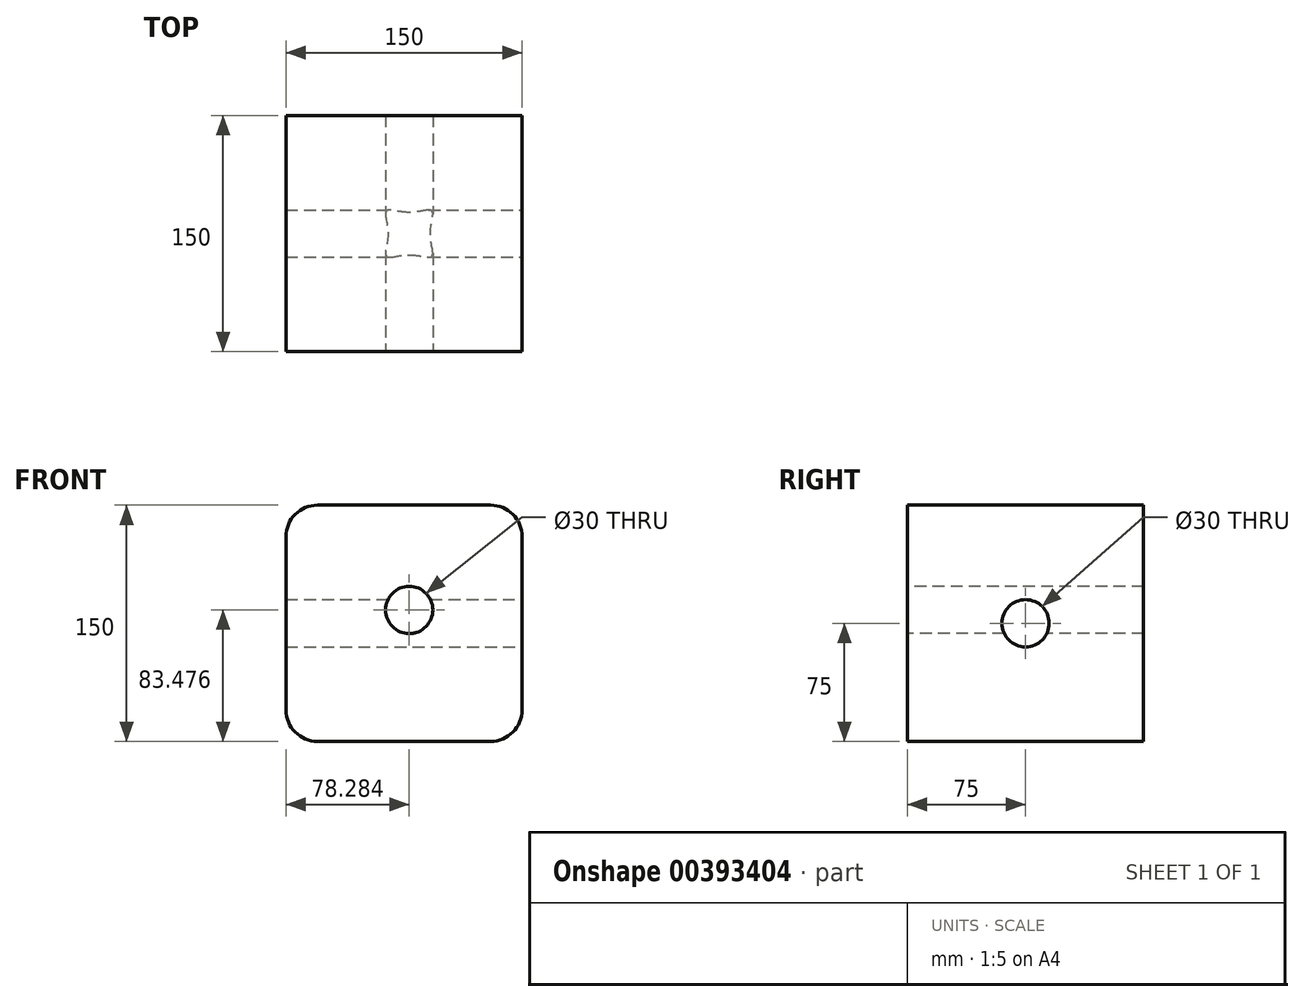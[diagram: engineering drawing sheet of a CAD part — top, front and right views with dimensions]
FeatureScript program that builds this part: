
annotation { "Feature Type Name" : "Feature", "Feature Type Description" : "" }
export const myFeature = defineFeature(function(context is Context, id is Id, definition is map)
    precondition{}
    {
        {
            var Q0;
            Q0=qCreatedBy(makeId("Front.planeOp"),FACE);
            var sketch = newSketch(context, id + "F0", { "sketchPlane" : qUnion([Q0])});
            skLineSegment(sketch, "E0.bottom", {"start": v(55, 75) * mm, "end": v(-55, 75) * mm});
            skLineSegment(sketch, "E0.top", {"start": v(55, -75) * mm, "end": v(-55, -75) * mm});
            skLineSegment(sketch, "E0.left", {"start": v(75, 55) * mm, "end": v(75, -55) * mm});
            skLineSegment(sketch, "E0.right", {"start": v(-75, 55) * mm, "end": v(-75, -55) * mm});
            skPoint(sketch, "E0.middle", {"position": v(0, 0) * mm});
            skPoint(sketch, "E1.visualSharp", {"position": v(-75, 75) * mm});
            skArc(sketch, "E1.filletArc", {"start": v(-55, 75) * mm, "mid": v(-69.14, 69.14) * mm, "end": v(-75, 55) * mm});
            skPoint(sketch, "E2.visualSharp", {"position": v(75, 75) * mm});
            skArc(sketch, "E2.filletArc", {"start": v(75, 55) * mm, "mid": v(69.14, 69.14) * mm, "end": v(55, 75) * mm});
            skPoint(sketch, "E3.visualSharp", {"position": v(75, -75) * mm});
            skArc(sketch, "E3.filletArc", {"start": v(55, -75) * mm, "mid": v(69.14, -69.14) * mm, "end": v(75, -55) * mm});
            skPoint(sketch, "E4.visualSharp", {"position": v(-75, -75) * mm});
            skArc(sketch, "E4.filletArc", {"start": v(-75, -55) * mm, "mid": v(-69.14, -69.14) * mm, "end": v(-55, -75) * mm});
            skSolve(sketch);
        }
        {
            var Q0;
            Q0 = qSketchRegion(id + "F0", true);
            extrude(context, id + "F1", {"entities" : qUnion([Q0]), "depth" : 150 * mm});
        }
        {
            var Q0;
            Q0=makeQuery(id+"F1.opExtrude","CAP_FACE",FACE,{"disambiguationData":[OSD([sQuery(id+"F0.wireOp",EDGE,"E0.bottom"),sQuery(id+"F0.wireOp",EDGE,"E0.top"),sQuery(id+"F0.wireOp",EDGE,"E0.left"),sQuery(id+"F0.wireOp",EDGE,"E0.right"),sQuery(id+"F0.wireOp",EDGE,"E1.filletArc"),sQuery(id+"F0.wireOp",EDGE,"E2.filletArc"),sQuery(id+"F0.wireOp",EDGE,"E3.filletArc"),sQuery(id+"F0.wireOp",EDGE,"E4.filletArc")])],"isStart":false});
            var sketch = newSketch(context, id + "F2", { "sketchPlane" : qUnion([Q0])});
            skCircle(sketch, "E5", {"center": v(3.28, 8.48) * mm, "radius": 15 * mm});
            skSolve(sketch);
        }
        {
            var Q0;
            Q0=sQuery(id+"F2.wireOp",VERTEX,"E5.center");
            var Q1;
            Q1=makeQuery(id+"F1.opExtrude","SWEPT_BODY",BODY,{"disambiguationData":[OSD([sQuery(id+"F0.wireOp",EDGE,"E0.bottom"),sQuery(id+"F0.wireOp",EDGE,"E0.top"),sQuery(id+"F0.wireOp",EDGE,"E0.left"),sQuery(id+"F0.wireOp",EDGE,"E0.right"),sQuery(id+"F0.wireOp",EDGE,"E1.filletArc"),sQuery(id+"F0.wireOp",EDGE,"E2.filletArc"),sQuery(id+"F0.wireOp",EDGE,"E3.filletArc"),sQuery(id+"F0.wireOp",EDGE,"E4.filletArc")])]});
            hole(context, id + "F3", {"style" : HoleStyle.SIMPLE, "endStyle" : HoleEndStyle.THROUGH, "holeDiameter" : 30 * mm, "isTappedThrough" : true, "tappedDepth" : 12 * mm, "tapClearance" : 3, "locations" : qUnion([Q0]), "scope" : qUnion([Q1])});
        }
        {
            var Q0;
            Q0=makeQuery(id+"F1.opExtrude","SWEPT_FACE",FACE,{"disambiguationData":[OSD([sQuery(id+"F0.wireOp",EDGE,"E0.left")])]});
            var sketch = newSketch(context, id + "F4", { "sketchPlane" : qUnion([Q0])});
            skCircle(sketch, "E6", {"center": v(-75, 0) * mm, "radius": 15 * mm});
            skPoint(sketch, "E6.centerSnap0", {"position": v(-75, 55) * mm});
            skPoint(sketch, "E6.centerSnap1", {"position": v(0, 0) * mm});
            skSolve(sketch);
        }
        {
            var Q0;
            Q0 = qSketchRegion(id + "F4", true);
            extrude(context, id + "F5", {"entities" : qUnion([Q0]), "operationType" : NewBodyOperationType.REMOVE, "oppositeDirection" : true, "depth" : 150 * mm});
        }
    });
